# Revit family: IS_Joy_A7378_BIM_GB
name_source: partatom
category: Plumbing Fixtures
revit_build: Autodesk Revit 2017 (Build: 20160225_1515(x64)
units: mm (PartAtom-declared; Revit-internal decimal feet)

## family parameters
Always vertical = No
Cut with Voids When Loaded = No
OmniClass Number = 23.45.55.17
OmniClass Title = Mixing Faucets
Part Type = Normal
Room Calculation Point = No
Round Connector Dimension = Use Diameter
Shared = No
Work Plane-Based = No

## types (4) — shared parameters
Accessories = https://www.idealstandard.co.uk
AssetType = Fixed
BIMObjectName = ISI_IdealStandard_Washbasin manual water supply sets_Joy_A7378
BarCode = 3800861086895
Brand = Ideal Standard
CurrencyUnit = £
Description = JOY BS2 Wall-mounted washbasin tap with round rosette and 180 mm Projection. Available in four different finishes, Chrome (AA), Silver storm (GN) 386, Brushed gold (A2) and Magnetic grey (A5)
DistributedBy = Ideal Standard
DurationUnit = Years
ExpectedLife = 30
FaucetFunction = MIXED
FaucetOperation = OTHER
FaucetType = OTHER
Features = BS2 Wall-mounted washbasin tap with round rosette and 180 mm Projection. Available in four different finishes, Chrome (AA), Silver storm (GN) 386, Brushed gold (A2) and Magnetic grey (A5)
Help = https://www.idealstandard.co.uk
IfcExportAs = IfcValveType
IfcExportType = FAUCET
Installation instructions = https://www.idealspec.co.uk
InstallationInstructions = https://www.idealstandard.co.uk
IsBuiltIn = No
MaintenanceInformation = https://www.idealstandard.co.uk
Manufacturer = Ideal Standard
ManufacturerURL = https://www.idealstandard.co.uk
Material = Brass
ModelNumber = A7378
NBS Reference Code = 45-35-70/371
NBS Reference Description = Water supply fittings for wash basins and troughs
Name = Washbasin manual water supply sets_Joy_A7378_IdealStandard
NettWeight = 1.81
NominalDepth = 285 mm  [stored 0.935039 ft]
NominalHeight = 55 mm  [stored 0.180446 ft]
NominalLength = 285 mm  [stored 0.935039 ft]
NominalWidth = 110 mm  [stored 0.360892 ft]
Product certification = https://www.idealstandard.co.uk
Product group = BASIN MIXER
ProductInformation = https://www.idealspec.co.uk
Shape = Sculptured
Size = 175 x 1889 x 106 mm
Space = Internal
SpareParts = https://www.idealspec.co.uk
SustainabilityPerformance = https://www.idealspec.co.uk
TestPressure = 10 Bar
URL = https://www.idealstandard.co.uk
Uniclass 2015 Code = Pr_40_20_87_96
Uniclass 2015 Name = Washbasin manual water supply sets
Uniclass2015Code = Pr_40_20_87_96
Uniclass2015Title = Washbasin manual water supply sets
Uniclass2015Version = v1.1
Version = 1
VolumeUnits = Litres
WRASURL = https://www.wras.co.uk
WarrantyDescription = Manufacturers Warranty
WarrantyDurationParts = 5
WarrantyDurationUnit = year
WarrantyGuarantorParts = https://www.idealspec.co.uk
WorkingPressure = 3bar
zero-valued in all types: InletConnectionSize, MaterialThickness

## per-type parameters (varying)
| type | Color | Finish | MainColor | Model | ModelReference |
| A7378A2 - JOY BSN MXR B-IN 180 5L CIRCUL KIT2 BR GOLD | Brushed Gold | Brushed Gold | Brushed Gold | A7378A2 | A7378A2 |
| A7378A5 - JOY BSN B-IN 180 5L CIRCUL KIT2 MGN GREY | Magnetic grey | Magnetic grey | Magnetic grey | A7378A5 | A7378A5 |
| A7378AA - JOY BSN MXR B-IN 180 5L CIRCUL KIT2 CHROME | Chrome | Chrome | Chrome | A7378AA | A7378AA |
| A7378GN - JOY BSN B-IN 180 5L CIRCUL KIT2 SILV STORM | Silver storm | Silver storm | Silver storm | A7378GN | A7378GN |

note: [stored X ft] marks values corroborated as IEEE doubles in the binary element streams (Revit-internal decimal feet)

## geometry (parser evidence)
native form markers: Sweep x3
no freeform markers — native parametric forms only
